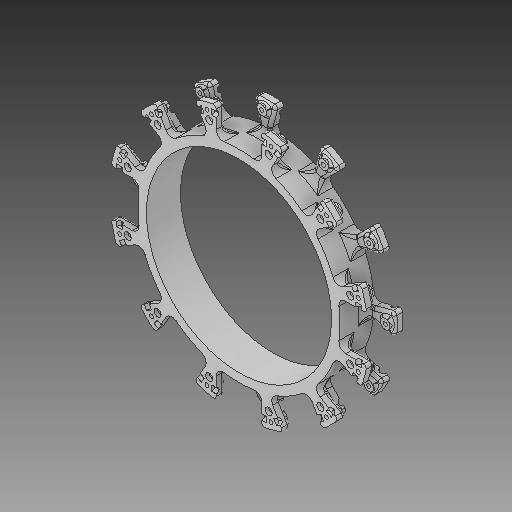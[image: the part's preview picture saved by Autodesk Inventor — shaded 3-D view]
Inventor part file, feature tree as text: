
AUTODESK INVENTOR PART (.ipt)
format: ipt  version: 2018 (Build 220112000, 112)  size: 2,134,016 bytes
history: native  units: in
note: dims shown in document units (in); Inventor stores cm internally (conversion verified against a paired STEP export)
features: fillet x1
ambient origin geometry x8: Origin, YZ Plane, XZ Plane, XY Plane, X Axis, Y Axis, Z Axis, Center Point
bodies: Solid1 (feature_tree)
feature tree (1):
  fillet  "Fillet17"  [1 undecoded]
note: 1 required parameter value undecoded (feature->parameter linkage not recoverable at this tier; creation-order binding heuristic only, values carry confidence <= 0.55)
